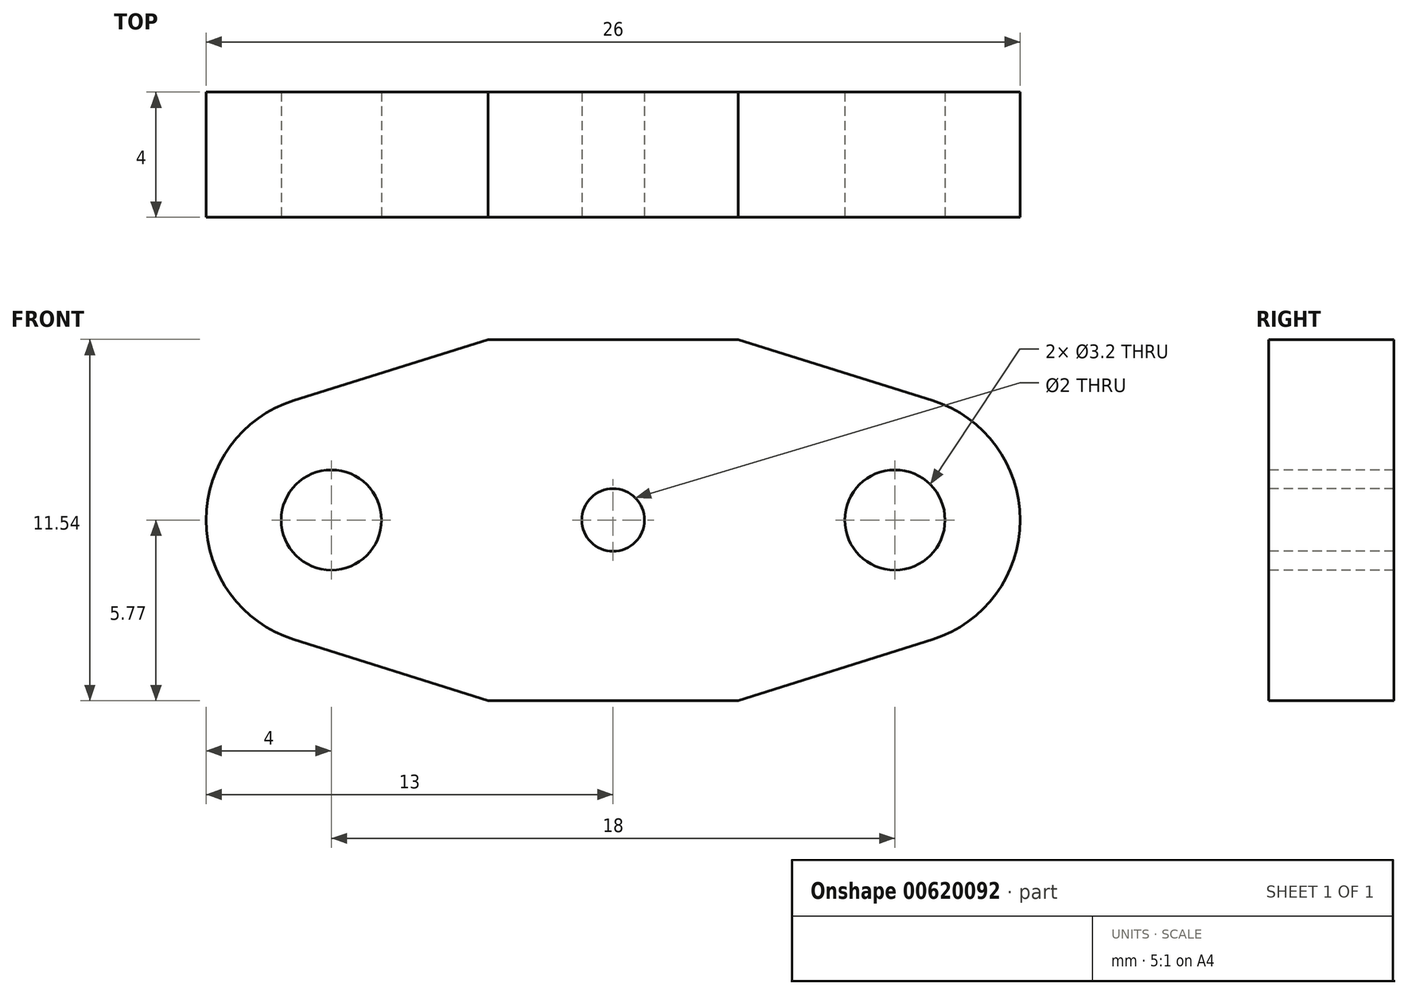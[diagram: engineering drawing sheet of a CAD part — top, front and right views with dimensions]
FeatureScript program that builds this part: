
annotation { "Feature Type Name" : "Feature", "Feature Type Description" : "" }
export const myFeature = defineFeature(function(context is Context, id is Id, definition is map)
    precondition{}
    {
        {
            var Q0;
            Q0=qCreatedBy(makeId("Front.planeOp"),FACE);
            var sketch = newSketch(context, id + "F0", { "sketchPlane" : qUnion([Q0])});
            skCircle(sketch, "E0", {"center": v(9, 0) * mm, "radius": 1.6 * mm, "construction": true});
            skCircle(sketch, "E1.MirrorC", {"center": v(-9, 0) * mm, "radius": 1.6 * mm, "construction": true});
            skArc(sketch, "E2", {"start": v(-10.2, 3.82) * mm, "mid": v(-13, 0) * mm, "end": v(-10.2, -3.82) * mm});
            skArc(sketch, "E3.MirrorC", {"start": v(10.2, 3.82) * mm, "mid": v(13, 0) * mm, "end": v(10.2, -3.82) * mm});
            skLineSegment(sketch, "E4.bottom", {"start": v(-4, 5.76) * mm, "end": v(4, 5.77) * mm});
            skLineSegment(sketch, "E4.top", {"start": v(-4, -5.77) * mm, "end": v(4, -5.77) * mm});
            skPoint(sketch, "E4.middle", {"position": v(0, 0) * mm});
            skLineSegment(sketch, "E5", {"start": v(-4, 5.76) * mm, "end": v(-10.2, 3.82) * mm});
            skLineSegment(sketch, "E6", {"start": v(-4, -5.77) * mm, "end": v(-10.2, -3.82) * mm});
            skLineSegment(sketch, "E7", {"start": v(4, -5.77) * mm, "end": v(10.2, -3.82) * mm});
            skLineSegment(sketch, "E8", {"start": v(4, 5.76) * mm, "end": v(10.2, 3.82) * mm});
            skSolve(sketch);
        }
        {
            var Q0;
            Q0 = qSketchRegion(id + "F0", true);
            extrude(context, id + "F1", {"entities" : qUnion([Q0]), "depth" : 4 * mm, "offsetDistance" : 25 * mm});
        }
        {
            var Q0;
            Q0=makeQuery(id+"F1.opExtrude","CAP_FACE",FACE,{"disambiguationData":[OSD([sQuery(id+"F0.wireOp",EDGE,"E2"),sQuery(id+"F0.wireOp",EDGE,"E3.MirrorC"),sQuery(id+"F0.wireOp",EDGE,"E4.bottom"),sQuery(id+"F0.wireOp",EDGE,"E4.top"),sQuery(id+"F0.wireOp",EDGE,"E5"),sQuery(id+"F0.wireOp",EDGE,"E6"),sQuery(id+"F0.wireOp",EDGE,"E7"),sQuery(id+"F0.wireOp",EDGE,"E8")])],"isStart":false});
            var sketch = newSketch(context, id + "F2", { "sketchPlane" : qUnion([Q0])});
            skCircle(sketch, "E9.0", {"center": v(-9, 0) * mm, "radius": 1.6 * mm});
            skCircle(sketch, "E10.0", {"center": v(9, 0) * mm, "radius": 1.6 * mm});
            skSolve(sketch);
        }
        {
            var Q0;
            Q0 = qSketchRegion(id + "F2", true);
            extrude(context, id + "F3", {"entities" : qUnion([Q0]), "operationType" : NewBodyOperationType.REMOVE, "endBound" : BoundingType.THROUGH_ALL, "oppositeDirection" : true, "depth" : 25 * mm, "offsetDistance" : 25 * mm});
        }
        {
            var Q0;
            Q0=makeQuery(id+"F1.opExtrude","CAP_FACE",FACE,{"disambiguationData":[OSD([sQuery(id+"F0.wireOp",EDGE,"E2"),sQuery(id+"F0.wireOp",EDGE,"E3.MirrorC"),sQuery(id+"F0.wireOp",EDGE,"E4.bottom"),sQuery(id+"F0.wireOp",EDGE,"E4.top"),sQuery(id+"F0.wireOp",EDGE,"E5"),sQuery(id+"F0.wireOp",EDGE,"E6"),sQuery(id+"F0.wireOp",EDGE,"E7"),sQuery(id+"F0.wireOp",EDGE,"E8")])],"isStart":false});
            var sketch = newSketch(context, id + "F4", { "sketchPlane" : qUnion([Q0])});
            skCircle(sketch, "E11", {"center": v(0, 0) * mm, "radius": 1 * mm});
            skSolve(sketch);
        }
        {
            var Q0;
            Q0 = qSketchRegion(id + "F4", true);
            extrude(context, id + "F5", {"entities" : qUnion([Q0]), "operationType" : NewBodyOperationType.REMOVE, "endBound" : BoundingType.THROUGH_ALL, "oppositeDirection" : true, "depth" : 25 * mm, "offsetDistance" : 25 * mm});
        }
    });
